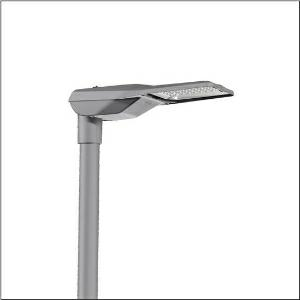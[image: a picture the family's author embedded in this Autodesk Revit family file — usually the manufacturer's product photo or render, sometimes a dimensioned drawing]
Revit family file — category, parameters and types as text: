
# Revit family: streetlight_sl_21_iq_mini___p0_8ab_5xe2r31v08hb_77c8
name_source: partatom
category: Lighting Fixtures
units: mm (PartAtom-declared; Revit-internal decimal feet)

## family parameters
Cut with Voids When Loaded = No
Host = Face
Light Source = No
Part Type = Normal
Room Calculation Point = No
Round Connector Dimension = Use Diameter
Shared = No

## types (1)
- --- (1 x LED, 8460 lm, 71 W, 3000K)
    Apparent Load = 71 VA
    CIE Flux Codes = 36 71 98 100 100
    Color Rendering = 70
    Color Temperature = 3000K
    Default Elevation = 1800 mm
    Description = Streetlight SL 21 iQ mini, mast luminaire, primary light control with lens, of PMMA, primary optical cover: cover, of toughened safety glass, transparent, light distribution: P0.8aB, light emission: direct distribution, primary light characteristic: asymmetric, installation type: post-top, side-entry, LED, High Power LED, rated luminous flux: 8.460lm, luminous efficacy: 119lm/W, light colour: 730, colour temperature: 3000K, control gear: iQ-Street Remote, D4i with power reduction, control: pre-setting: logarithmic dimming characteristic, Street-Remote, Auto-Match, Temp-Guard, Lumen-Switch, Night-Set, Smart-Wire, Light-Fading, Desk-Remote (wireless, voltage-free reading and setting of iQ features in the workshop via application-optimized NFC function/RFID function), optimised constant luminous flux control (CLO 2.0), mains connection: 220..240V, AC, 50/60Hz, start of lifetime: 71W, end of service life: 75W, reduction: 30W, luminaire housing, of diecast aluminium, powder-coated, SITECO metallic grey (DB 702S), corrosivity category C5 high according to DIN EN ISO 12944, please order mast flange separately, inclination adjustable: 0°, 5°, 10°, 15°, sealing non-destructively replaceable, multi-level sealing system, length: 628mm, width: 235mm, height: 110mm, mast flange for spigot size: 42mm (side-entry): 5XC10008XM4, 60/48mm (side-entry/post-top): 5XC10108XM2, 76/60mm (side-entry/post-top): 5XC10108XM1, mounting height: 4..8m, Smart Interface above, protection rating (complete): IP66, insulation class (complete): insulation class II (safety insulation), certification: CE, ENEC, ENEC+, VDE, impact resistance: IK10, permissible operating ambient temperature for outdoor applications: -40..+50°C, standard-compliant lighting for roads and squares, packaging unit: 1 piece

Light Distribution: P0.8aB
    Height = 110 mm
    Lamp = 1 x LED
    Lamp Light Flux = 8460 lm
    Lamp Power = 71 W
    Lamp count = 1
    Length = 625 mm
    Luminous efficacy = 119 lm/W
    Manufacturer = Siteco
    ModVariant = No
    Model = 5XE2R31V08HB
    Number of Poles = 1
    OnlyDefault = Yes
    Power Factor = 1
    Product Name = Streetlight SL 21 iQ mini | P0.8aB
    Product group = mast luminaire | pylon top
    ProductGroupID = 6100
    Protection Class = Protection class II
    Protection Degree = IP 66
    RLX_Detail_Level = 1
    RLX_Emergency_Light_Flux = 0 lm
    RLX_Emergency_Type = 0
    RLX_Emergency_Type_DB = No
    RlxData = <blob elided: 92149 chars, md5=f7b13c63>
    Socket = socket
    Standby Power = 0 W
    System Light Flux = 8460 lm
    System Power = 71 W
    Type Comments = factory setting: luminous flux: 100 % | dim-lin: 254 | 716 mA
    Type Image = l_1003515.jpg
    URL = http://relux.com
    VarID = @adj_083129
    Voltage = 0 V
    Weight = 0.00 kg
    Width = 234 mm

## geometry (parser evidence)
native form markers: Blend x4, Sweep x11
no freeform markers — native parametric forms only
